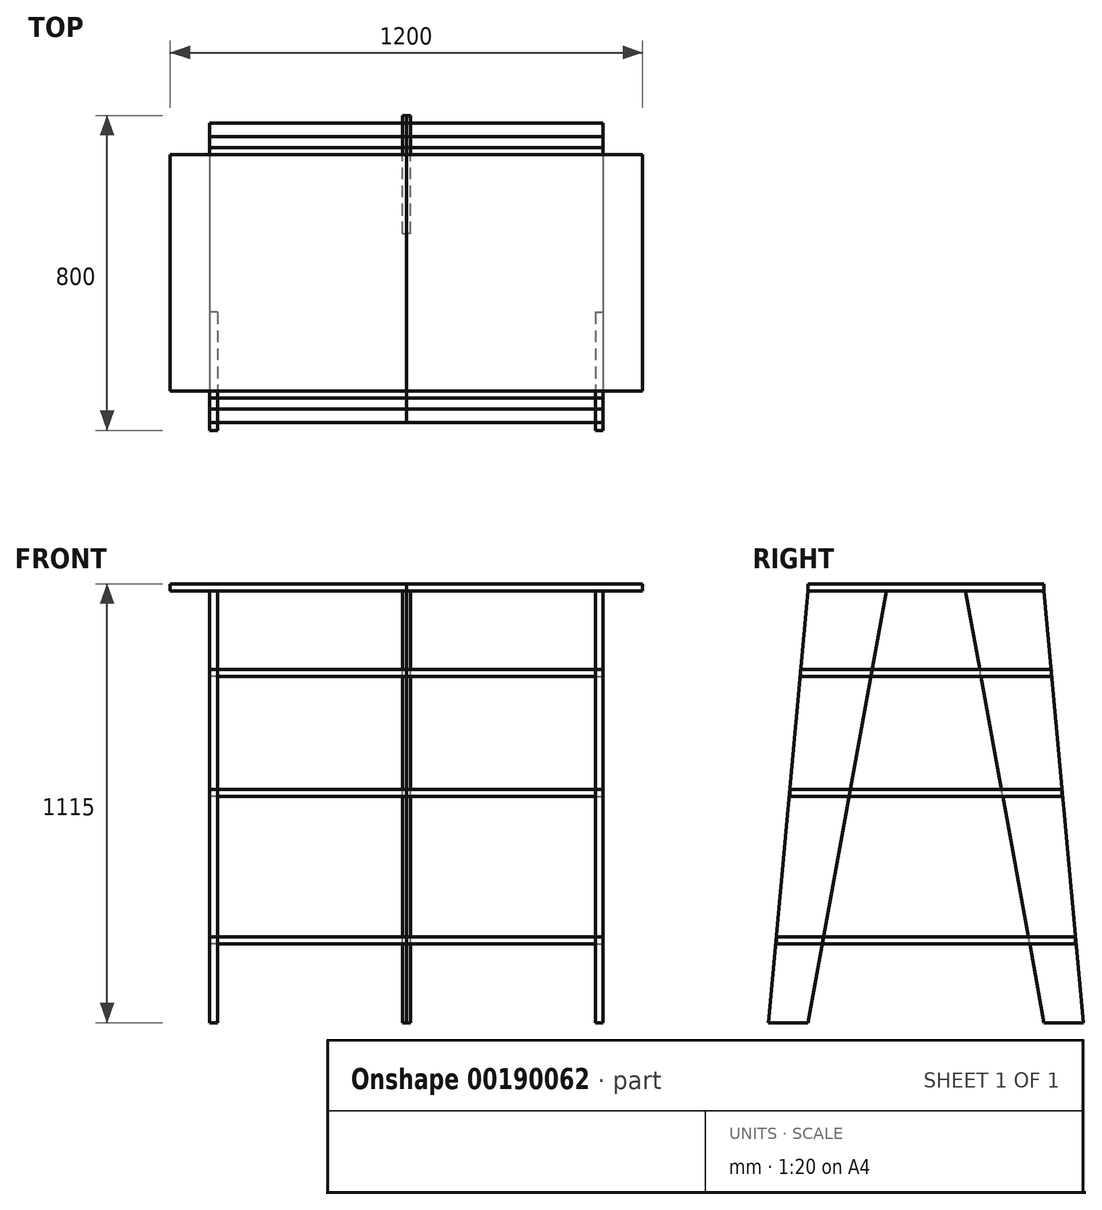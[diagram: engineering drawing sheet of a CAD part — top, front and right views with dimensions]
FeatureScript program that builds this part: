
annotation { "Feature Type Name" : "Feature", "Feature Type Description" : "" }
export const myFeature = defineFeature(function(context is Context, id is Id, definition is map)
    precondition{}
    {
        {
            var Q0;
            Q0=qCreatedBy(makeId("Front.planeOp"),FACE);
            var sketch = newSketch(context, id + "F0", { "sketchPlane" : qUnion([Q0])});
            skLineSegment(sketch, "E0.bottom", {"start": v(-600, 1115) * mm, "end": v(0, 1115) * mm});
            skLineSegment(sketch, "E0.top", {"start": v(-600, 1097) * mm, "end": v(0, 1097) * mm});
            skLineSegment(sketch, "E0.left", {"start": v(-600, 1115) * mm, "end": v(-600, 1097) * mm});
            skLineSegment(sketch, "E0.right", {"start": v(0, 1115) * mm, "end": v(0, 1097) * mm});
            skSolve(sketch);
        }
        {
            var Q0;
            Q0 = qSketchRegion(id + "F0", true);
            extrude(context, id + "F1", {"entities" : qUnion([Q0]), "depth" : 600 * mm});
        }
        {
            var Q0;
            Q0=qCreatedBy(makeId("Right.planeOp"),FACE);
            cPlane(context, id + "F2", {"entities" : qUnion([Q0]), "cplaneType" : CPlaneType.OFFSET, "offset" : 500 * mm, "oppositeDirection" : true, "width" : 150 * mm, "height" : 150 * mm});
        }
        {
            var Q0;
            Q0=qCreatedBy(id+"F2.planeOp",FACE);
            var sketch = newSketch(context, id + "F3", { "sketchPlane" : qUnion([Q0])});
            skLineSegment(sketch, "E1", {"start": v(-400, 1097) * mm, "end": v(-600, 1097) * mm});
            skLineSegment(sketch, "E2", {"start": v(-600, 1097) * mm, "end": v(-700, 0) * mm});
            skLineSegment(sketch, "E3", {"start": v(-700, 0) * mm, "end": v(-600, 0) * mm});
            skLineSegment(sketch, "E4", {"start": v(-600, 0) * mm, "end": v(-400, 1097) * mm});
            skSolve(sketch);
        }
        {
            var Q0;
            Q0 = qSketchRegion(id + "F3", true);
            extrude(context, id + "F4", {"entities" : qUnion([Q0]), "operationType" : NewBodyOperationType.ADD, "depth" : 20 * mm});
        }
        {
            var Q0;
            Q0=qCreatedBy(makeId("Right.planeOp"),FACE);
            var sketch = newSketch(context, id + "F5", { "sketchPlane" : qUnion([Q0])});
            skLineSegment(sketch, "E5", {"start": v(0, 1097) * mm, "end": v(100, 0) * mm});
            skLineSegment(sketch, "E6", {"start": v(100, 0) * mm, "end": v(0, 0) * mm});
            skLineSegment(sketch, "E7", {"start": v(0, 0) * mm, "end": v(-200, 1097) * mm});
            skLineSegment(sketch, "E8", {"start": v(-200, 1097) * mm, "end": v(0, 1097) * mm});
            skSolve(sketch);
        }
        {
            var Q0;
            Q0 = qSketchRegion(id + "F5", true);
            extrude(context, id + "F6", {"entities" : qUnion([Q0]), "oppositeDirection" : true, "depth" : 10 * mm});
        }
        {
            var Q0;
            Q0=qCreatedBy(id+"F2.planeOp",FACE);
            var sketch = newSketch(context, id + "F7", { "sketchPlane" : qUnion([Q0])});
            skLineSegment(sketch, "E9.bottom", {"start": v(45.94, 593) * mm, "end": v(-645.94, 593) * mm});
            skLineSegment(sketch, "E9.top", {"start": v(45.94, 575) * mm, "end": v(-645.94, 575) * mm});
            skLineSegment(sketch, "E9.left", {"start": v(45.94, 593) * mm, "end": v(45.94, 575) * mm});
            skLineSegment(sketch, "E9.right", {"start": v(-645.94, 593) * mm, "end": v(-645.94, 575) * mm});
            skLineSegment(sketch, "E10.bottom", {"start": v(18.23, 897) * mm, "end": v(-618.23, 897) * mm});
            skLineSegment(sketch, "E10.top", {"start": v(18.23, 879) * mm, "end": v(-618.23, 879) * mm});
            skLineSegment(sketch, "E10.left", {"start": v(18.23, 897) * mm, "end": v(18.23, 879) * mm});
            skLineSegment(sketch, "E10.right", {"start": v(-618.23, 897) * mm, "end": v(-618.23, 879) * mm});
            skLineSegment(sketch, "E11.bottom", {"start": v(80.13, 218) * mm, "end": v(-680.13, 218) * mm});
            skLineSegment(sketch, "E11.top", {"start": v(80.13, 200) * mm, "end": v(-680.13, 200) * mm});
            skLineSegment(sketch, "E11.left", {"start": v(80.13, 218) * mm, "end": v(80.13, 200) * mm});
            skLineSegment(sketch, "E11.right", {"start": v(-680.13, 218) * mm, "end": v(-680.13, 200) * mm});
            skSolve(sketch);
        }
        {
            var Q0;
            Q0 = qSketchRegion(id + "F7", true);
            extrude(context, id + "F8", {"entities" : qUnion([Q0]), "depth" : 500 * mm});
        }
        {
            var Q0;
            Q0=makeQuery(id+"F8.opExtrude","SWEPT_BODY",BODY,{"disambiguationData":[OSD([sQuery(id+"F7.wireOp",EDGE,"E9.bottom"),sQuery(id+"F7.wireOp",EDGE,"E9.top"),sQuery(id+"F7.wireOp",EDGE,"E9.left"),sQuery(id+"F7.wireOp",EDGE,"E9.right")])]});
            var Q1;
            Q1=makeQuery(id+"F8.opExtrude","SWEPT_BODY",BODY,{"disambiguationData":[OSD([sQuery(id+"F7.wireOp",EDGE,"E10.bottom"),sQuery(id+"F7.wireOp",EDGE,"E10.top"),sQuery(id+"F7.wireOp",EDGE,"E10.left"),sQuery(id+"F7.wireOp",EDGE,"E10.right")])]});
            var Q2;
            Q2=makeQuery(id+"F8.opExtrude","SWEPT_BODY",BODY,{"disambiguationData":[OSD([sQuery(id+"F7.wireOp",EDGE,"E11.bottom"),sQuery(id+"F7.wireOp",EDGE,"E11.top"),sQuery(id+"F7.wireOp",EDGE,"E11.left"),sQuery(id+"F7.wireOp",EDGE,"E11.right")])]});
            var Q3;
            Q3=makeQuery(id+"F1.opExtrude","SWEPT_BODY",BODY,{"disambiguationData":[OSD([sQuery(id+"F0.wireOp",EDGE,"E0.bottom"),sQuery(id+"F0.wireOp",EDGE,"E0.top"),sQuery(id+"F0.wireOp",EDGE,"E0.left"),sQuery(id+"F0.wireOp",EDGE,"E0.right")])]});
            var Q4;
            Q4=makeQuery(id+"F6.opExtrude","SWEPT_BODY",BODY,{"disambiguationData":[OSD([sQuery(id+"F5.wireOp",EDGE,"E5"),sQuery(id+"F5.wireOp",EDGE,"E6"),sQuery(id+"F5.wireOp",EDGE,"E7"),sQuery(id+"F5.wireOp",EDGE,"E8")])]});
            var Q5;
            Q5=qCreatedBy(makeId("Right.planeOp"),FACE);
            mirror(context, id + "F9", {"entities" : qUnion([Q0, Q1, Q2, Q3, Q4]), "mirrorPlane" : qUnion([Q5])});
        }
    });
